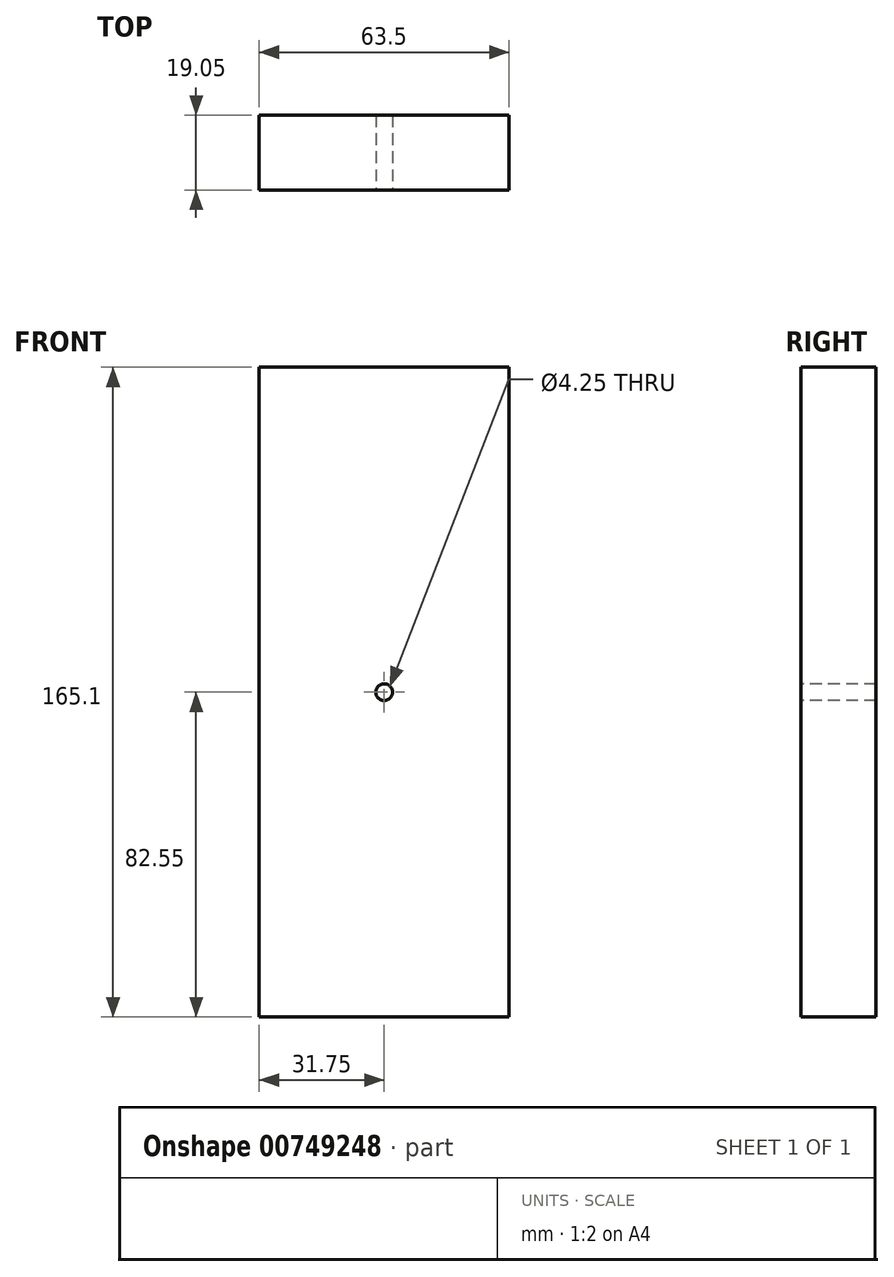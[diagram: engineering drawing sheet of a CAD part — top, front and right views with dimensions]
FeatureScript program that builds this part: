
annotation { "Feature Type Name" : "Feature", "Feature Type Description" : "" }
export const myFeature = defineFeature(function(context is Context, id is Id, definition is map)
    precondition{}
    {
        {
            var Q0;
            Q0=qCreatedBy(makeId("Front.planeOp"),FACE);
            var sketch = newSketch(context, id + "F0", { "sketchPlane" : qUnion([Q0])});
            skLineSegment(sketch, "E0.bottom", {"start": v(31.75, 82.55) * mm, "end": v(-31.75, 82.55) * mm});
            skLineSegment(sketch, "E0.top", {"start": v(31.75, -82.55) * mm, "end": v(-31.75, -82.55) * mm});
            skLineSegment(sketch, "E0.left", {"start": v(31.75, 82.55) * mm, "end": v(31.75, -82.55) * mm});
            skLineSegment(sketch, "E0.right", {"start": v(-31.75, 82.55) * mm, "end": v(-31.75, -82.55) * mm});
            skPoint(sketch, "E0.middle", {"position": v(0, 0) * mm});
            skSolve(sketch);
        }
        {
            var Q0;
            Q0 = qSketchRegion(id + "F0", true);
            extrude(context, id + "F1", {"entities" : qUnion([Q0]), "depth" : 19.05 * mm, "offsetDistance" : 25.4 * mm});
        }
        {
            var Q0;
            Q0=makeQuery(id+"F1.opExtrude","CAP_FACE",FACE,{"disambiguationData":[OSD([sQuery(id+"F0.wireOp",EDGE,"E0.bottom"),sQuery(id+"F0.wireOp",EDGE,"E0.top"),sQuery(id+"F0.wireOp",EDGE,"E0.left"),sQuery(id+"F0.wireOp",EDGE,"E0.right")])],"isStart":false});
            var sketch = newSketch(context, id + "F2", { "sketchPlane" : qUnion([Q0])});
            skLineSegment(sketch, "E1", {"start": v(-31.75, 82.55) * mm, "end": v(31.75, -82.55) * mm, "construction": true});
            skCircle(sketch, "E2", {"center": v(0, 0) * mm, "radius": 2.13 * mm});
            skSolve(sketch);
        }
        {
            var Q0;
            Q0 = qSketchRegion(id + "F2", true);
            extrude(context, id + "F3", {"entities" : qUnion([Q0]), "operationType" : NewBodyOperationType.REMOVE, "endBound" : BoundingType.THROUGH_ALL, "oppositeDirection" : true, "depth" : 25.4 * mm, "offsetDistance" : 25.4 * mm});
        }
    });
